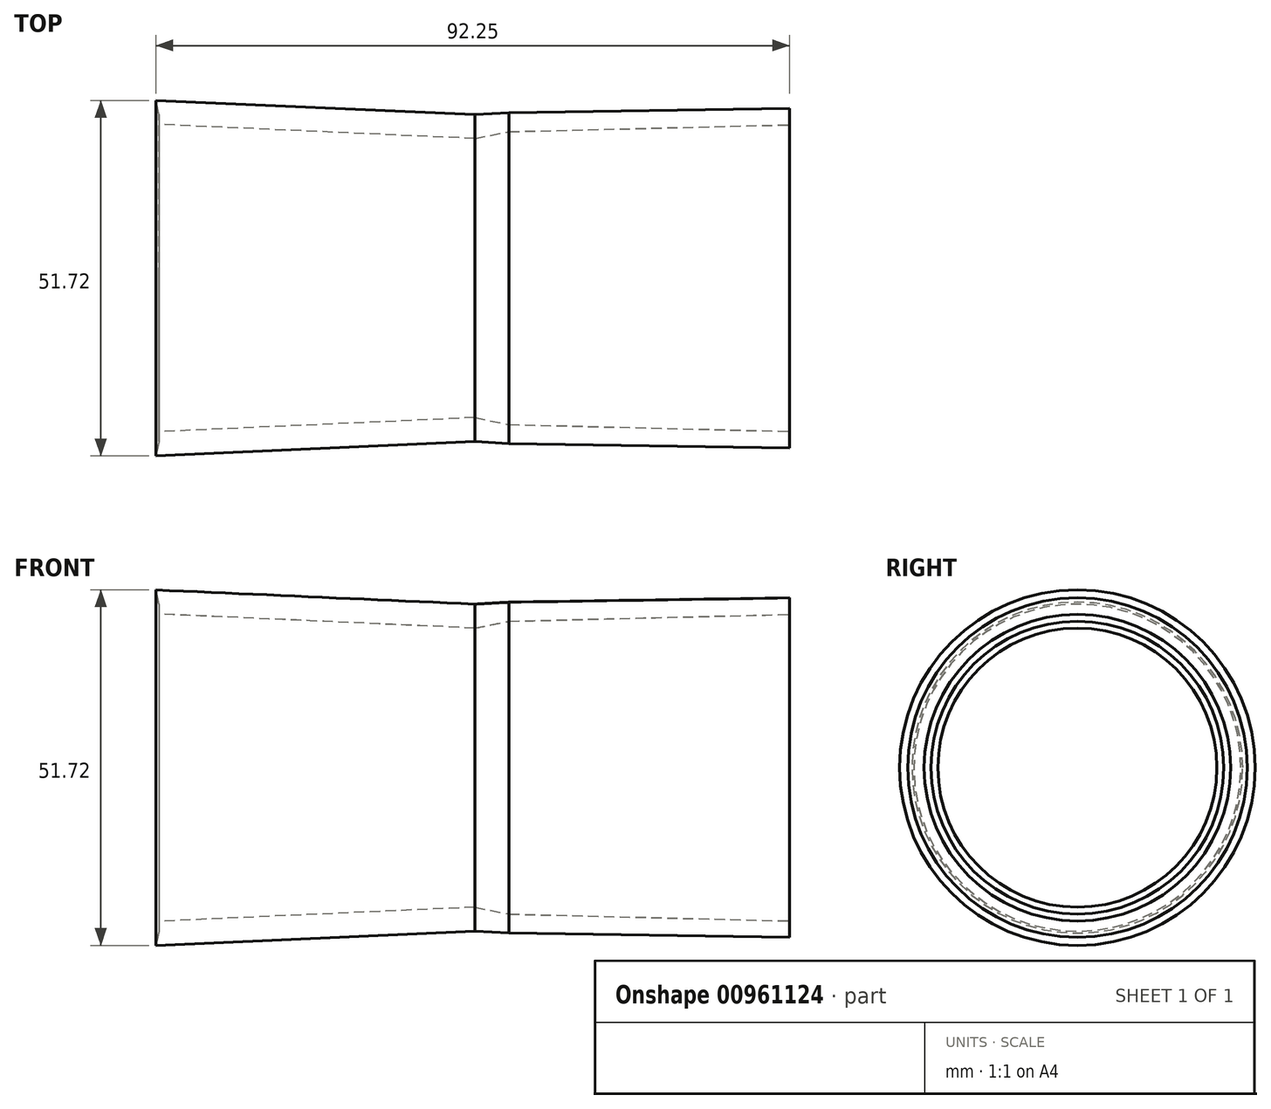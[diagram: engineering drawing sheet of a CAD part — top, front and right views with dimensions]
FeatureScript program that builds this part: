
annotation { "Feature Type Name" : "Feature", "Feature Type Description" : "" }
export const myFeature = defineFeature(function(context is Context, id is Id, definition is map)
    precondition{}
    {
        {
            var Q0;
            Q0=qCreatedBy(makeId("Top.planeOp"),FACE);
            var sketch = newSketch(context, id + "F0", { "sketchPlane" : qUnion([Q0])});
            skLineSegment(sketch, "E0", {"start": v(-16.92, 21.3) * mm, "end": v(-21.91, 20.3) * mm});
            skLineSegment(sketch, "E1", {"start": v(-67.87, 22.35) * mm, "end": v(-67.87, 23.79) * mm});
            skLineSegment(sketch, "E2", {"start": v(-21.91, 23.79) * mm, "end": v(-16.92, 24.07) * mm});
            skLineSegment(sketch, "E3", {"start": v(-43.34, 0) * mm, "end": v(39.1, 0) * mm, "construction": true});
            skPoint(sketch, "E4", {"position": v(-21.91, 20.3) * mm});
            skLineSegment(sketch, "E5", {"start": v(-16.92, 24.07) * mm, "end": v(23.88, 24.7) * mm});
            skLineSegment(sketch, "E6", {"start": v(23.88, 24.7) * mm, "end": v(23.91, 22.3) * mm});
            skLineSegment(sketch, "E7", {"start": v(23.91, 22.3) * mm, "end": v(-16.92, 21.3) * mm});
            skPoint(sketch, "E8", {"position": v(23.91, 22.3) * mm});
            skPoint(sketch, "E9", {"position": v(3.5, 21.8) * mm});
            skPoint(sketch, "E10", {"position": v(-16.92, 21.3) * mm});
            skLineSegment(sketch, "E11", {"start": v(23.91, 22.3) * mm, "end": v(23.91, 0) * mm, "construction": true});
            skLineSegment(sketch, "E12", {"start": v(-16.92, 21.3) * mm, "end": v(-16.92, 0) * mm, "construction": true});
            skLineSegment(sketch, "E13", {"start": v(-67.87, 22.35) * mm, "end": v(-67.87, 0) * mm, "construction": true});
            skLineSegment(sketch, "E14", {"start": v(-67.87, 22.35) * mm, "end": v(-21.91, 20.3) * mm});
            skLineSegment(sketch, "E15", {"start": v(-21.91, 20.3) * mm, "end": v(-21.91, 0) * mm});
            skLineSegment(sketch, "E16", {"start": v(-21.91, 23.79) * mm, "end": v(-68.34, 25.86) * mm});
            skLineSegment(sketch, "E17", {"start": v(-68.34, 25.86) * mm, "end": v(-67.87, 23.79) * mm});
            skSolve(sketch);
        }
        {
            var Q0;
            Q0=makeQuery(id+"F0.imprint","IMPRINT",FACE,{"disambiguationData":[TD([[makeQuery(id+"F0.imprint","IMPRINT",EDGE,{"derivedFrom":sQuery(id+"F0.wireOp",EDGE,"E0")}),-1.0]])]});
            var Q1;
            Q1=sQuery(id+"F0.wireOp",EDGE,"E3");
            revolve(context, id + "F1", {"surfaceOperationType" : NewSurfaceOperationType.NEW, "entities" : qUnion([Q0]), "axis" : qUnion([Q1]), "revolveType" : RevolveType.FULL});
        }
    });
